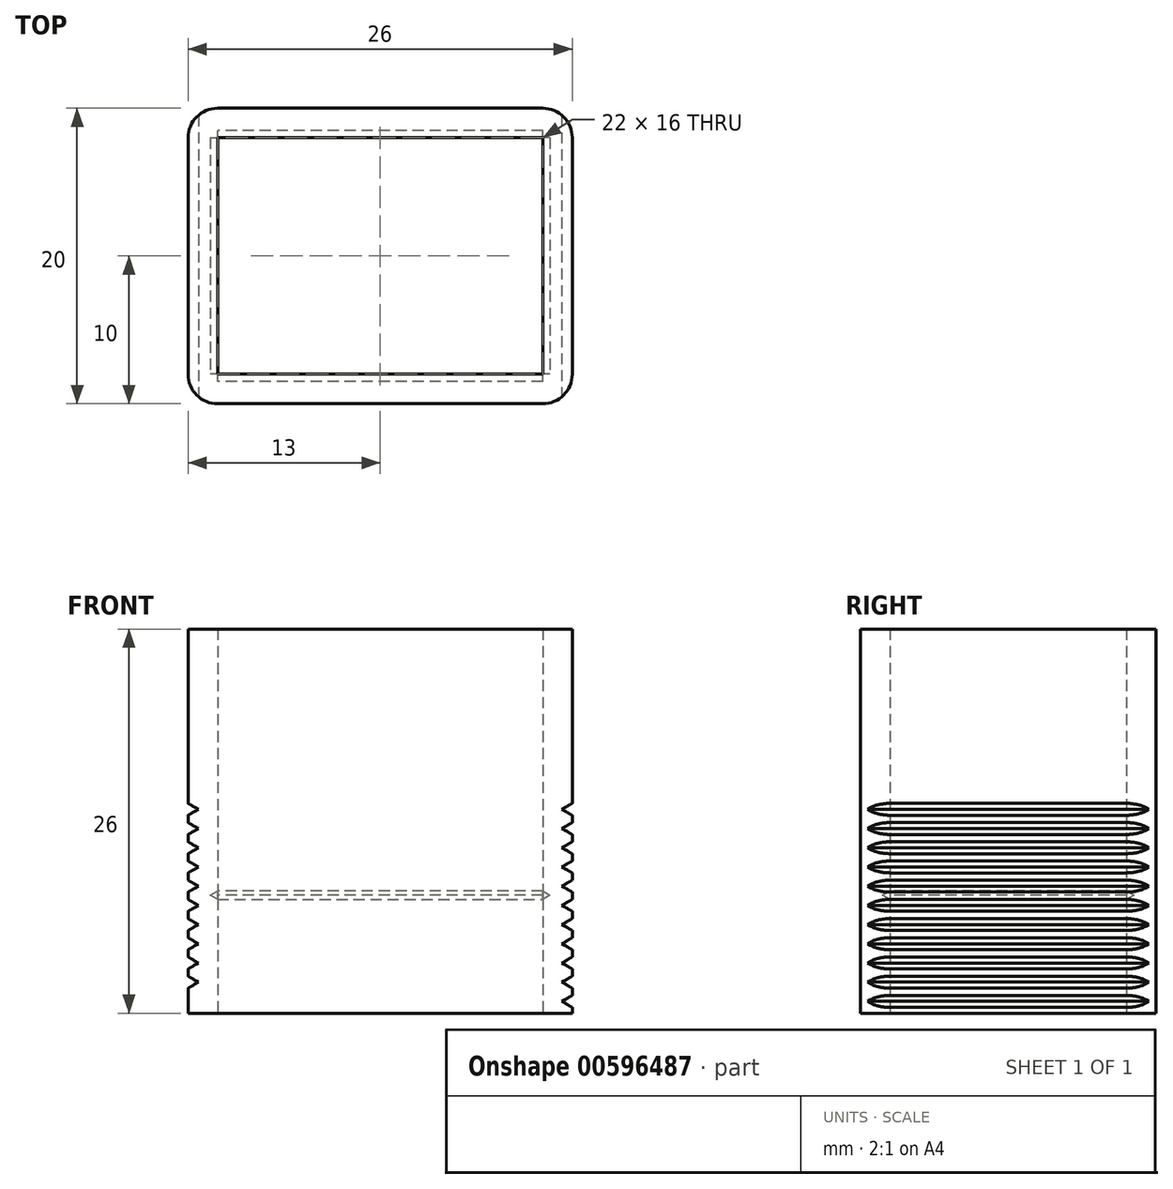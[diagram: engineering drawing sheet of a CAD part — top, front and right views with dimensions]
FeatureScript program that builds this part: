
annotation { "Feature Type Name" : "Feature", "Feature Type Description" : "" }
export const myFeature = defineFeature(function(context is Context, id is Id, definition is map)
    precondition{}
    {
        {
            var Q0;
            Q0=qCreatedBy(makeId("Top.planeOp"),FACE);
            var sketch = newSketch(context, id + "F0", { "sketchPlane" : qUnion([Q0])});
            skLineSegment(sketch, "E0.bottom", {"start": v(0, 0) * mm, "end": v(22, 0) * mm});
            skLineSegment(sketch, "E0.top", {"start": v(0, 16) * mm, "end": v(22, 16) * mm});
            skLineSegment(sketch, "E0.left", {"start": v(0, 0) * mm, "end": v(0, 16) * mm});
            skLineSegment(sketch, "E0.right", {"start": v(22, 0) * mm, "end": v(22, 16) * mm});
            skSolve(sketch);
        }
        {
            var Q0;
            Q0=makeQuery(id+"F0.imprint","IMPRINT",FACE,{"disambiguationData":[TD([[makeQuery(id+"F0.imprint","IMPRINT",EDGE,{"derivedFrom":sQuery(id+"F0.wireOp",EDGE,"E0.bottom")}),1.0]])]});
            extrude(context, id + "F1", {"entities" : qUnion([Q0]), "depth" : 28 * mm, "offsetDistance" : 25 * mm, "hasSecondDirection" : true, "secondDirectionOppositeDirection" : false, "secondDirectionDepth" : 4 * mm});
        }
        {
            var Q0;
            Q0=makeQuery(id+"F1.opExtrude","CAP_FACE",FACE,{"disambiguationData":[OSD([sQuery(id+"F0.wireOp",EDGE,"E0.bottom"),sQuery(id+"F0.wireOp",EDGE,"E0.top"),sQuery(id+"F0.wireOp",EDGE,"E0.left"),sQuery(id+"F0.wireOp",EDGE,"E0.right")])],"isStart":false});
            shell(context, id + "F2", {"entities" : qUnion([Q0]), "thickness" : 2 * mm, "oppositeDirection" : true});
        }
        {
            var Q0;
            Q0=makeQuery(id+"F1.opExtrude","SWEPT_FACE",FACE,{"disambiguationData":[OSD([sQuery(id+"F0.wireOp",EDGE,"E0.left")])]});
            var sketch = newSketch(context, id + "F3", { "sketchPlane" : qUnion([Q0])});
            skLineSegment(sketch, "E1.0", {"start": v(-16, 28) * mm, "end": v(-16, 4) * mm});
            skLineSegment(sketch, "E2.0", {"start": v(0, 28) * mm, "end": v(0, 4) * mm});
            skLineSegment(sketch, "E3.0", {"start": v(0, 0) * mm, "end": v(-16, 0) * mm});
            skLineSegment(sketch, "E4", {"start": v(-16, 10) * mm, "end": v(0, 10) * mm});
            skCircle(sketch, "E5.cCircle", {"center": v(-16, 10) * mm, "radius": 0.25 * mm, "construction": true});
            skLineSegment(sketch, "E5.0", {"start": v(-15.75, 10.43) * mm, "end": v(-15.75, 9.57) * mm});
            skLineSegment(sketch, "E5.1", {"start": v(-15.75, 9.57) * mm, "end": v(-16.5, 10) * mm});
            skLineSegment(sketch, "E5.2", {"start": v(-16.5, 10) * mm, "end": v(-15.75, 10.43) * mm});
            skPoint(sketch, "E5.0.midPoint", {"position": v(-15.75, 10) * mm});
            skCircle(sketch, "E6.cCircle", {"center": v(0, 10) * mm, "radius": 0.25 * mm, "construction": true});
            skLineSegment(sketch, "E6.0", {"start": v(-0.25, 9.57) * mm, "end": v(-0.25, 10.43) * mm});
            skLineSegment(sketch, "E6.1", {"start": v(-0.25, 10.43) * mm, "end": v(0.5, 10) * mm});
            skLineSegment(sketch, "E6.2", {"start": v(0.5, 10) * mm, "end": v(-0.25, 9.57) * mm});
            skPoint(sketch, "E6.0.midPoint", {"position": v(-0.25, 10) * mm});
            skSolve(sketch);
        }
        {
            var Q0;
            {var subQ0=sQuery(id+"F3.wireOp",EDGE,"E1.0");var subQ1=makeQuery(id+"F3.imprint","INTERSECT",VERTEX,{"derivedFrom":[subQ0,sQuery(id+"F3.wireOp",EDGE,"E4")]});Q0=makeQuery(id+"F3.imprint","IMPRINT",FACE,{"disambiguationData":[TD([[makeQuery(id+"F3.imprint","IMPRINT",EDGE,{"disambiguationData":[TD([[subQ1,1.0]])],"derivedFrom":subQ0}),-1.0]])]});}
            var Q1;
            {var subQ0=sQuery(id+"F3.wireOp",EDGE,"E4");var subQ1=sQuery(id+"F3.wireOp",EDGE,"E1.0");var subQ2=makeQuery(id+"F3.imprint","INTERSECT",VERTEX,{"derivedFrom":[subQ1,subQ0]});Q1=makeQuery(id+"F3.imprint","IMPRINT",FACE,{"disambiguationData":[TD([[makeQuery(id+"F3.imprint","IMPRINT",EDGE,{"disambiguationData":[TD([[subQ2,1.0]])],"derivedFrom":subQ1}),1.0]])]});}
            var Q2;
            {var subQ0=sQuery(id+"F3.wireOp",EDGE,"E4");var subQ1=sQuery(id+"F3.wireOp",EDGE,"E1.0");var subQ2=makeQuery(id+"F3.imprint","INTERSECT",VERTEX,{"derivedFrom":[subQ1,subQ0]});Q2=makeQuery(id+"F3.imprint","IMPRINT",FACE,{"disambiguationData":[TD([[makeQuery(id+"F3.imprint","IMPRINT",EDGE,{"disambiguationData":[TD([[subQ2,-1.0]])],"derivedFrom":subQ1}),1.0]])]});}
            var Q3;
            {var subQ0=sQuery(id+"F3.wireOp",EDGE,"E4");var subQ1=sQuery(id+"F3.wireOp",EDGE,"E2.0");var subQ2=makeQuery(id+"F3.imprint","INTERSECT",VERTEX,{"derivedFrom":[subQ1,subQ0]});Q3=makeQuery(id+"F3.imprint","IMPRINT",FACE,{"disambiguationData":[TD([[makeQuery(id+"F3.imprint","IMPRINT",EDGE,{"disambiguationData":[TD([[subQ2,1.0]])],"derivedFrom":subQ1}),-1.0]])]});}
            var Q4;
            {var subQ0=sQuery(id+"F3.wireOp",EDGE,"E4");var subQ1=sQuery(id+"F3.wireOp",EDGE,"E2.0");var subQ2=makeQuery(id+"F3.imprint","INTERSECT",VERTEX,{"derivedFrom":[subQ1,subQ0]});Q4=makeQuery(id+"F3.imprint","IMPRINT",FACE,{"disambiguationData":[TD([[makeQuery(id+"F3.imprint","IMPRINT",EDGE,{"disambiguationData":[TD([[subQ2,-1.0]])],"derivedFrom":subQ1}),-1.0]])]});}
            var Q5;
            {var subQ0=sQuery(id+"F3.wireOp",EDGE,"E2.0");var subQ1=makeQuery(id+"F3.imprint","INTERSECT",VERTEX,{"derivedFrom":[subQ0,sQuery(id+"F3.wireOp",EDGE,"E4")]});Q5=makeQuery(id+"F3.imprint","IMPRINT",FACE,{"disambiguationData":[TD([[makeQuery(id+"F3.imprint","IMPRINT",EDGE,{"disambiguationData":[TD([[subQ1,1.0]])],"derivedFrom":subQ0}),1.0]])]});}
            var Q6;
            Q6=makeQuery(id+"F2.opShell","OFFSET_FACE",FACE,{"disambiguationData":[OSD([sQuery(id+"F0.wireOp",EDGE,"E0.right")])]});
            var Q7;
            Q7=makeQuery(id+"F2.opShell","OFFSET_FACE",FACE,{"disambiguationData":[OSD([sQuery(id+"F0.wireOp",EDGE,"E0.left")])]});
            extrude(context, id + "F4", {"entities" : qUnion([Q0, Q1, Q2, Q3, Q4, Q5]), "operationType" : NewBodyOperationType.REMOVE, "endBound" : BoundingType.UP_TO_SURFACE, "oppositeDirection" : true, "depth" : 25 * mm, "endBoundEntityFace" : qUnion([Q6]), "offsetDistance" : 25 * mm, "hasSecondDirection" : true, "secondDirectionBound" : BoundingType.UP_TO_SURFACE, "secondDirectionOppositeDirection" : true, "secondDirectionDepth" : 25 * mm, "secondDirectionBoundEntityFace" : qUnion([Q7])});
        }
        {
            var Q0;
            Q0=makeQuery(id+"F1.opExtrude","SWEPT_FACE",FACE,{"disambiguationData":[OSD([sQuery(id+"F0.wireOp",EDGE,"E0.bottom")])]});
            var sketch = newSketch(context, id + "F5", { "sketchPlane" : qUnion([Q0])});
            skLineSegment(sketch, "E7.0", {"start": v(0, 9.71) * mm, "end": v(0, 10) * mm});
            skLineSegment(sketch, "E8.0", {"start": v(0, 10) * mm, "end": v(0, 10.29) * mm});
            skLineSegment(sketch, "E9.0", {"start": v(22, 9.71) * mm, "end": v(22, 10) * mm});
            skLineSegment(sketch, "E10.0", {"start": v(22, 10) * mm, "end": v(22, 10.29) * mm});
            skLineSegment(sketch, "E11.0", {"start": v(22, 10) * mm, "end": v(0, 10) * mm});
            skCircle(sketch, "E12.cCircle", {"center": v(0, 10) * mm, "radius": 0.25 * mm, "construction": true});
            skLineSegment(sketch, "E12.0", {"start": v(0.25, 10.43) * mm, "end": v(0.25, 9.57) * mm});
            skLineSegment(sketch, "E12.1", {"start": v(0.25, 9.57) * mm, "end": v(-0.5, 10) * mm});
            skLineSegment(sketch, "E12.2", {"start": v(-0.5, 10) * mm, "end": v(0.25, 10.43) * mm});
            skPoint(sketch, "E12.0.midPoint", {"position": v(0.25, 10) * mm});
            skCircle(sketch, "E13.cCircle", {"center": v(22, 10) * mm, "radius": 0.25 * mm, "construction": true});
            skLineSegment(sketch, "E13.0", {"start": v(21.75, 9.57) * mm, "end": v(21.75, 10.43) * mm});
            skLineSegment(sketch, "E13.1", {"start": v(21.75, 10.43) * mm, "end": v(22.5, 10) * mm});
            skLineSegment(sketch, "E13.2", {"start": v(22.5, 10) * mm, "end": v(21.75, 9.57) * mm});
            skPoint(sketch, "E13.0.midPoint", {"position": v(21.75, 10) * mm});
            skLineSegment(sketch, "E14", {"start": v(24, 8) * mm, "end": v(-2, 8) * mm, "construction": true});
            skCircle(sketch, "E15.cCircle", {"center": v(-2, 8) * mm, "radius": 0.35 * mm, "construction": true});
            skLineSegment(sketch, "E15.0", {"start": v(-2.35, 7.4) * mm, "end": v(-2.35, 8.6) * mm});
            skLineSegment(sketch, "E15.1", {"start": v(-2.35, 8.6) * mm, "end": v(-1.3, 8) * mm});
            skLineSegment(sketch, "E15.2", {"start": v(-1.3, 8) * mm, "end": v(-2.35, 7.4) * mm});
            skPoint(sketch, "E15.0.midPoint", {"position": v(-2.35, 8) * mm});
            skLineSegment(sketch, "E16.0", {"start": v(-2, 28) * mm, "end": v(-2, 4) * mm});
            skLineSegment(sketch, "E17.0.1.0", {"start": v(-2.35, 8.7) * mm, "end": v(-2.35, 9.9) * mm});
            skCircle(sketch, "E17.0.1.1", {"center": v(-2, 9.3) * mm, "radius": 0.35 * mm, "construction": true});
            skPoint(sketch, "E17.0.1.2", {"position": v(-2.35, 9.3) * mm});
            skLineSegment(sketch, "E17.0.1.3", {"start": v(-1.3, 9.3) * mm, "end": v(-2.35, 8.7) * mm});
            skLineSegment(sketch, "E17.0.1.4", {"start": v(-2.35, 9.9) * mm, "end": v(-1.3, 9.3) * mm});
            skLineSegment(sketch, "E17.0.2.0", {"start": v(-2.35, 10) * mm, "end": v(-2.35, 11.2) * mm});
            skCircle(sketch, "E17.0.2.1", {"center": v(-2, 10.6) * mm, "radius": 0.35 * mm, "construction": true});
            skPoint(sketch, "E17.0.2.2", {"position": v(-2.35, 10.6) * mm});
            skLineSegment(sketch, "E17.0.2.3", {"start": v(-1.3, 10.6) * mm, "end": v(-2.35, 10) * mm});
            skLineSegment(sketch, "E17.0.2.4", {"start": v(-2.35, 11.2) * mm, "end": v(-1.3, 10.6) * mm});
            skLineSegment(sketch, "E17.0.3.0", {"start": v(-2.35, 11.3) * mm, "end": v(-2.35, 12.5) * mm});
            skCircle(sketch, "E17.0.3.1", {"center": v(-2, 11.9) * mm, "radius": 0.35 * mm, "construction": true});
            skPoint(sketch, "E17.0.3.2", {"position": v(-2.35, 11.9) * mm});
            skLineSegment(sketch, "E17.0.3.3", {"start": v(-1.3, 11.9) * mm, "end": v(-2.35, 11.3) * mm});
            skLineSegment(sketch, "E17.0.3.4", {"start": v(-2.35, 12.5) * mm, "end": v(-1.3, 11.9) * mm});
            skLineSegment(sketch, "E17.0.4.0", {"start": v(-2.35, 12.6) * mm, "end": v(-2.35, 13.8) * mm});
            skCircle(sketch, "E17.0.4.1", {"center": v(-2, 13.2) * mm, "radius": 0.35 * mm, "construction": true});
            skPoint(sketch, "E17.0.4.2", {"position": v(-2.35, 13.2) * mm});
            skLineSegment(sketch, "E17.0.4.3", {"start": v(-1.3, 13.2) * mm, "end": v(-2.35, 12.6) * mm});
            skLineSegment(sketch, "E17.0.4.4", {"start": v(-2.35, 13.8) * mm, "end": v(-1.3, 13.2) * mm});
            skLineSegment(sketch, "E17.0.5.0", {"start": v(-2.35, 13.9) * mm, "end": v(-2.35, 15.1) * mm});
            skCircle(sketch, "E17.0.5.1", {"center": v(-2, 14.5) * mm, "radius": 0.35 * mm, "construction": true});
            skPoint(sketch, "E17.0.5.2", {"position": v(-2.35, 14.5) * mm});
            skLineSegment(sketch, "E17.0.5.3", {"start": v(-1.3, 14.5) * mm, "end": v(-2.35, 13.9) * mm});
            skLineSegment(sketch, "E17.0.5.4", {"start": v(-2.35, 15.1) * mm, "end": v(-1.3, 14.5) * mm});
            skLineSegment(sketch, "E17.direction1", {"start": v(-2.35, 8) * mm, "end": v(1.16, 8) * mm, "construction": true});
            skLineSegment(sketch, "E17.direction2", {"start": v(-2.35, 8) * mm, "end": v(-2.35, 9.3) * mm, "construction": true});
            skLineSegment(sketch, "E18.0.0.6", {"start": v(-2.35, 15.2) * mm, "end": v(-2.35, 16.4) * mm});
            skCircle(sketch, "E18.3.0.6", {"center": v(-2, 15.8) * mm, "radius": 0.35 * mm, "construction": true});
            skPoint(sketch, "E18.5.0.6", {"position": v(-2.35, 15.8) * mm});
            skLineSegment(sketch, "E18.6.0.6", {"start": v(-1.3, 15.8) * mm, "end": v(-2.35, 15.2) * mm});
            skLineSegment(sketch, "E18.9.0.6", {"start": v(-2.35, 16.4) * mm, "end": v(-1.3, 15.8) * mm});
            skLineSegment(sketch, "E19.MirrorCS", {"start": v(-1.3, 5.4) * mm, "end": v(-2.35, 6) * mm});
            skLineSegment(sketch, "E20.MirrorCS", {"start": v(-1.3, 4.1) * mm, "end": v(-2.35, 4.7) * mm});
            skLineSegment(sketch, "E21.MirrorCS", {"start": v(-2.35, 4.8) * mm, "end": v(-1.3, 5.4) * mm});
            skLineSegment(sketch, "E22.MirrorCS", {"start": v(-2.35, 6.1) * mm, "end": v(-1.3, 6.7) * mm});
            skLineSegment(sketch, "E23.MirrorCS", {"start": v(-2.35, 3.5) * mm, "end": v(-1.3, 4.1) * mm});
            skLineSegment(sketch, "E24.MirrorCS", {"start": v(-2.35, 2.2) * mm, "end": v(-1.3, 2.8) * mm});
            skLineSegment(sketch, "E25.MirrorCS", {"start": v(-2.35, 2.1) * mm, "end": v(-2.35, 0.9) * mm});
            skLineSegment(sketch, "E26.MirrorCS", {"start": v(-2.35, 0.8) * mm, "end": v(-2.35, -0.4) * mm});
            skLineSegment(sketch, "E27.MirrorCS", {"start": v(-1.3, 0.2) * mm, "end": v(-2.35, 0.8) * mm});
            skLineSegment(sketch, "E28.MirrorCS", {"start": v(-2.35, 4.7) * mm, "end": v(-2.35, 3.5) * mm});
            skCircle(sketch, "E29.MirrorC", {"center": v(-2, 6.7) * mm, "radius": 0.35 * mm, "construction": true});
            skCircle(sketch, "E30.MirrorC", {"center": v(-2, 1.5) * mm, "radius": 0.35 * mm, "construction": true});
            skCircle(sketch, "E31.MirrorC", {"center": v(-2, 5.4) * mm, "radius": 0.35 * mm, "construction": true});
            skLineSegment(sketch, "E32.MirrorCS", {"start": v(-2.35, 3.4) * mm, "end": v(-2.35, 2.2) * mm});
            skCircle(sketch, "E33.MirrorC", {"center": v(-2, 4.1) * mm, "radius": 0.35 * mm, "construction": true});
            skLineSegment(sketch, "E34.MirrorCS", {"start": v(-2.35, 0.9) * mm, "end": v(-1.3, 1.5) * mm});
            skLineSegment(sketch, "E35.MirrorCS", {"start": v(-1.3, 2.8) * mm, "end": v(-2.35, 3.4) * mm});
            skLineSegment(sketch, "E36.MirrorCS", {"start": v(-2.35, 6) * mm, "end": v(-2.35, 4.8) * mm});
            skLineSegment(sketch, "E37.MirrorCS", {"start": v(-1.3, 6.7) * mm, "end": v(-2.35, 7.3) * mm});
            skCircle(sketch, "E38.MirrorC", {"center": v(-2, 0.2) * mm, "radius": 0.35 * mm, "construction": true});
            skLineSegment(sketch, "E39.MirrorCS", {"start": v(-2.35, 7.3) * mm, "end": v(-2.35, 6.1) * mm});
            skPoint(sketch, "E40.MirrorP", {"position": v(-2.35, 0.2) * mm});
            skCircle(sketch, "E41.MirrorC", {"center": v(-2, 2.8) * mm, "radius": 0.35 * mm, "construction": true});
            skPoint(sketch, "E42.MirrorP", {"position": v(-2.35, 1.5) * mm});
            skPoint(sketch, "E43.MirrorP", {"position": v(-2.35, 6.7) * mm});
            skPoint(sketch, "E44.MirrorP", {"position": v(-2.35, 5.4) * mm});
            skLineSegment(sketch, "E45.MirrorCS", {"start": v(-2.35, -0.4) * mm, "end": v(-1.3, 0.2) * mm});
            skLineSegment(sketch, "E46.MirrorCS", {"start": v(-1.3, 1.5) * mm, "end": v(-2.35, 2.1) * mm});
            skPoint(sketch, "E47.MirrorP", {"position": v(-2.35, 2.8) * mm});
            skPoint(sketch, "E48.MirrorP", {"position": v(-2.35, 4.1) * mm});
            skLineSegment(sketch, "E49", {"start": v(11, 18) * mm, "end": v(11, -2) * mm, "construction": true});
            skLineSegment(sketch, "E50.MirrorCS", {"start": v(24.35, 11.3) * mm, "end": v(24.35, 12.5) * mm});
            skLineSegment(sketch, "E51.MirrorCS", {"start": v(24.35, 8.7) * mm, "end": v(24.35, 9.9) * mm});
            skLineSegment(sketch, "E52.MirrorCS", {"start": v(24.35, 10) * mm, "end": v(24.35, 11.2) * mm});
            skLineSegment(sketch, "E53.MirrorCS", {"start": v(24.35, 4.7) * mm, "end": v(24.35, 3.5) * mm});
            skLineSegment(sketch, "E54.MirrorCS", {"start": v(24.35, 6) * mm, "end": v(24.35, 4.8) * mm});
            skLineSegment(sketch, "E55.MirrorCS", {"start": v(24.35, 12.6) * mm, "end": v(24.35, 13.8) * mm});
            skLineSegment(sketch, "E56.MirrorCS", {"start": v(24.35, 7.4) * mm, "end": v(24.35, 8.6) * mm});
            skLineSegment(sketch, "E57.MirrorCS", {"start": v(23.3, 11.9) * mm, "end": v(24.35, 11.3) * mm});
            skCircle(sketch, "E58.MirrorC", {"center": v(24, 11.9) * mm, "radius": 0.35 * mm, "construction": true});
            skLineSegment(sketch, "E59.MirrorCS", {"start": v(24.35, 8.6) * mm, "end": v(23.3, 8) * mm});
            skCircle(sketch, "E60.MirrorC", {"center": v(24, 10.6) * mm, "radius": 0.35 * mm, "construction": true});
            skLineSegment(sketch, "E61.MirrorCS", {"start": v(24.35, 7.3) * mm, "end": v(24.35, 6.1) * mm});
            skLineSegment(sketch, "E62.MirrorCS", {"start": v(24.35, 8) * mm, "end": v(24.35, 9.3) * mm, "construction": true});
            skCircle(sketch, "E63.MirrorC", {"center": v(24, 8) * mm, "radius": 0.35 * mm, "construction": true});
            skLineSegment(sketch, "E64.MirrorCS", {"start": v(23.3, 10.6) * mm, "end": v(24.35, 10) * mm});
            skCircle(sketch, "E65.MirrorC", {"center": v(24, 2.8) * mm, "radius": 0.35 * mm, "construction": true});
            skLineSegment(sketch, "E66.MirrorCS", {"start": v(24.35, 2.2) * mm, "end": v(23.3, 2.8) * mm});
            skLineSegment(sketch, "E67.MirrorCS", {"start": v(24.35, 13.8) * mm, "end": v(23.3, 13.2) * mm});
            skCircle(sketch, "E68.MirrorC", {"center": v(24, 4.1) * mm, "radius": 0.35 * mm, "construction": true});
            skLineSegment(sketch, "E69.MirrorCS", {"start": v(23.3, 15.8) * mm, "end": v(24.35, 15.2) * mm});
            skLineSegment(sketch, "E70.MirrorCS", {"start": v(24.35, -0.4) * mm, "end": v(23.3, 0.2) * mm});
            skLineSegment(sketch, "E71.MirrorCS", {"start": v(24.35, 2.1) * mm, "end": v(24.35, 0.9) * mm});
            skLineSegment(sketch, "E72.MirrorCS", {"start": v(24.35, 13.9) * mm, "end": v(24.35, 15.1) * mm});
            skCircle(sketch, "E73.MirrorC", {"center": v(24, 9.3) * mm, "radius": 0.35 * mm, "construction": true});
            skLineSegment(sketch, "E74.MirrorCS", {"start": v(23.3, 1.5) * mm, "end": v(24.35, 2.1) * mm});
            skLineSegment(sketch, "E75.MirrorCS", {"start": v(23.3, 2.8) * mm, "end": v(24.35, 3.4) * mm});
            skLineSegment(sketch, "E76.MirrorCS", {"start": v(23.3, 5.4) * mm, "end": v(24.35, 6) * mm});
            skPoint(sketch, "E77.MirrorP", {"position": v(24.35, 4.1) * mm});
            skLineSegment(sketch, "E78.MirrorCS", {"start": v(24.35, 11.2) * mm, "end": v(23.3, 10.6) * mm});
            skPoint(sketch, "E79.MirrorP", {"position": v(24.35, 13.2) * mm});
            skLineSegment(sketch, "E80.MirrorCS", {"start": v(24.35, 3.4) * mm, "end": v(24.35, 2.2) * mm});
            skLineSegment(sketch, "E81.MirrorCS", {"start": v(24.35, 0.8) * mm, "end": v(24.35, -0.4) * mm});
            skCircle(sketch, "E82.MirrorC", {"center": v(24, 14.5) * mm, "radius": 0.35 * mm, "construction": true});
            skLineSegment(sketch, "E83.MirrorCS", {"start": v(23.3, 14.5) * mm, "end": v(24.35, 13.9) * mm});
            skLineSegment(sketch, "E84.MirrorCS", {"start": v(24.35, 0.9) * mm, "end": v(23.3, 1.5) * mm});
            skLineSegment(sketch, "E85.MirrorCS", {"start": v(24.35, 3.5) * mm, "end": v(23.3, 4.1) * mm});
            skPoint(sketch, "E86.MirrorP", {"position": v(24.35, 6.7) * mm});
            skLineSegment(sketch, "E87.MirrorCS", {"start": v(24.35, 15.1) * mm, "end": v(23.3, 14.5) * mm});
            skCircle(sketch, "E88.MirrorC", {"center": v(24, 15.8) * mm, "radius": 0.35 * mm, "construction": true});
            skLineSegment(sketch, "E89.MirrorCS", {"start": v(24.35, 9.9) * mm, "end": v(23.3, 9.3) * mm});
            skCircle(sketch, "E90.MirrorC", {"center": v(24, 1.5) * mm, "radius": 0.35 * mm, "construction": true});
            skLineSegment(sketch, "E91.MirrorCS", {"start": v(24.35, 15.2) * mm, "end": v(24.35, 16.4) * mm});
            skCircle(sketch, "E92.MirrorC", {"center": v(24, 6.7) * mm, "radius": 0.35 * mm, "construction": true});
            skLineSegment(sketch, "E93.MirrorCS", {"start": v(23.3, 4.1) * mm, "end": v(24.35, 4.7) * mm});
            skLineSegment(sketch, "E94.MirrorCS", {"start": v(23.3, 0.2) * mm, "end": v(24.35, 0.8) * mm});
            skLineSegment(sketch, "E95.MirrorCS", {"start": v(23.3, 13.2) * mm, "end": v(24.35, 12.6) * mm});
            skCircle(sketch, "E96.MirrorC", {"center": v(24, 5.4) * mm, "radius": 0.35 * mm, "construction": true});
            skCircle(sketch, "E97.MirrorC", {"center": v(24, 13.2) * mm, "radius": 0.35 * mm, "construction": true});
            skLineSegment(sketch, "E98.MirrorCS", {"start": v(23.3, 9.3) * mm, "end": v(24.35, 8.7) * mm});
            skPoint(sketch, "E99.MirrorP", {"position": v(24.35, 5.4) * mm});
            skPoint(sketch, "E100.MirrorP", {"position": v(24.35, 11.9) * mm});
            skPoint(sketch, "E101.MirrorP", {"position": v(24.35, 10.6) * mm});
            skLineSegment(sketch, "E102.MirrorCS", {"start": v(24.35, 12.5) * mm, "end": v(23.3, 11.9) * mm});
            skLineSegment(sketch, "E103.MirrorCS", {"start": v(24.35, 6.1) * mm, "end": v(23.3, 6.7) * mm});
            skLineSegment(sketch, "E104.MirrorCS", {"start": v(23.3, 6.7) * mm, "end": v(24.35, 7.3) * mm});
            skLineSegment(sketch, "E105.MirrorCS", {"start": v(24.35, 4.8) * mm, "end": v(23.3, 5.4) * mm});
            skCircle(sketch, "E106.MirrorC", {"center": v(24, 0.2) * mm, "radius": 0.35 * mm, "construction": true});
            skLineSegment(sketch, "E107.MirrorCS", {"start": v(23.3, 8) * mm, "end": v(24.35, 7.4) * mm});
            skLineSegment(sketch, "E108.MirrorCS", {"start": v(24.35, 16.4) * mm, "end": v(23.3, 15.8) * mm});
            skPoint(sketch, "E109.MirrorP", {"position": v(24.35, 14.5) * mm});
            skPoint(sketch, "E110.MirrorP", {"position": v(24.35, 8) * mm});
            skPoint(sketch, "E111.MirrorP", {"position": v(24.35, 0.2) * mm});
            skPoint(sketch, "E112.MirrorP", {"position": v(24.35, 1.5) * mm});
            skPoint(sketch, "E113.MirrorP", {"position": v(24.35, 2.8) * mm});
            skPoint(sketch, "E114.MirrorP", {"position": v(24.35, 15.8) * mm});
            skPoint(sketch, "E115.MirrorP", {"position": v(24.35, 9.3) * mm});
            skSolve(sketch);
        }
        {
            var Q0;
            {var subQ0=sQuery(id+"F5.wireOp",EDGE,"E7.0");Q0=makeQuery(id+"F5.imprint","IMPRINT",FACE,{"disambiguationData":[TD([[makeQuery(id+"F5.imprint","IMPRINT",EDGE,{"derivedFrom":subQ0}),1.0]])]});}
            var Q1;
            {var subQ0=sQuery(id+"F5.wireOp",EDGE,"E8.0");Q1=makeQuery(id+"F5.imprint","IMPRINT",FACE,{"disambiguationData":[TD([[makeQuery(id+"F5.imprint","IMPRINT",EDGE,{"derivedFrom":subQ0}),-1.0]])]});}
            var Q2;
            {var subQ0=sQuery(id+"F5.wireOp",EDGE,"E7.0");Q2=makeQuery(id+"F5.imprint","IMPRINT",FACE,{"disambiguationData":[TD([[makeQuery(id+"F5.imprint","IMPRINT",EDGE,{"derivedFrom":subQ0}),-1.0]])]});}
            var Q3;
            {var subQ0=sQuery(id+"F5.wireOp",EDGE,"E9.0");Q3=makeQuery(id+"F5.imprint","IMPRINT",FACE,{"disambiguationData":[TD([[makeQuery(id+"F5.imprint","IMPRINT",EDGE,{"derivedFrom":subQ0}),-1.0]])]});}
            var Q4;
            {var subQ0=sQuery(id+"F5.wireOp",EDGE,"E10.0");Q4=makeQuery(id+"F5.imprint","IMPRINT",FACE,{"disambiguationData":[TD([[makeQuery(id+"F5.imprint","IMPRINT",EDGE,{"derivedFrom":subQ0}),1.0]])]});}
            var Q5;
            {var subQ0=sQuery(id+"F5.wireOp",EDGE,"E9.0");Q5=makeQuery(id+"F5.imprint","IMPRINT",FACE,{"disambiguationData":[TD([[makeQuery(id+"F5.imprint","IMPRINT",EDGE,{"derivedFrom":subQ0}),1.0]])]});}
            var Q6;
            {var subQ2=sQuery(id+"F0.wireOp",EDGE,"E0.top");Q6=makeQuery(id+"F4.boolean.opBoolean","SPLIT",FACE,{"disambiguationData":[TD([makeQuery(id+"F4.opExtrude","SWEPT_FACE",FACE,{"disambiguationData":[OSD([sQuery(id+"F3.wireOp",EDGE,"E5.2")])]})])],"derivedFrom":makeQuery(id+"F2.opShell","OFFSET_FACE",FACE,{"disambiguationData":[OSD([subQ2])]})});}
            var Q7;
            {var subQ2=sQuery(id+"F0.wireOp",EDGE,"E0.bottom");Q7=makeQuery(id+"F4.boolean.opBoolean","SPLIT",FACE,{"disambiguationData":[TD([makeQuery(id+"F4.opExtrude","SWEPT_FACE",FACE,{"disambiguationData":[OSD([sQuery(id+"F3.wireOp",EDGE,"E6.1")])]})])],"derivedFrom":makeQuery(id+"F2.opShell","OFFSET_FACE",FACE,{"disambiguationData":[OSD([subQ2])]})});}
            extrude(context, id + "F6", {"entities" : qUnion([Q0, Q1, Q2, Q3, Q4, Q5]), "operationType" : NewBodyOperationType.REMOVE, "endBound" : BoundingType.UP_TO_SURFACE, "oppositeDirection" : true, "depth" : 25 * mm, "endBoundEntityFace" : qUnion([Q6]), "offsetDistance" : 25 * mm, "hasSecondDirection" : true, "secondDirectionBound" : BoundingType.UP_TO_SURFACE, "secondDirectionOppositeDirection" : true, "secondDirectionDepth" : 25 * mm, "secondDirectionBoundEntityFace" : qUnion([Q7])});
        }
        {
            var Q0;
            Q0=makeQuery(id+"F1.opExtrude","SWEPT_EDGE",EDGE,{"disambiguationData":[OSD([sQuery(id+"F0.wireOp",EDGE,"E0.bottom"),sQuery(id+"F0.wireOp",EDGE,"E0.right")])]});
            var Q1;
            Q1=makeQuery(id+"F1.opExtrude","SWEPT_EDGE",EDGE,{"disambiguationData":[OSD([sQuery(id+"F0.wireOp",EDGE,"E0.top"),sQuery(id+"F0.wireOp",EDGE,"E0.right")])]});
            var Q2;
            Q2=makeQuery(id+"F1.opExtrude","SWEPT_EDGE",EDGE,{"disambiguationData":[OSD([sQuery(id+"F0.wireOp",EDGE,"E0.bottom"),sQuery(id+"F0.wireOp",EDGE,"E0.left")])]});
            var Q3;
            Q3=makeQuery(id+"F1.opExtrude","SWEPT_EDGE",EDGE,{"disambiguationData":[OSD([sQuery(id+"F0.wireOp",EDGE,"E0.top"),sQuery(id+"F0.wireOp",EDGE,"E0.left")])]});
            fillet(context, id + "F7", {"entities" : qUnion([Q0, Q1, Q2, Q3]), "radius" : 2 * mm, "tangentPropagation" : true, "allowEdgeOverflow" : false});
        }
        {
            var Q0;
            {var subQ0=sQuery(id+"F5.wireOp",EDGE,"E108.MirrorCS");var subQ1=sQuery(id+"F5.wireOp",EDGE,"E69.MirrorCS");var subQ2=makeQuery(id+"F5.imprint","INTERSECT",VERTEX,{"derivedFrom":[subQ1,subQ0]});Q0=makeQuery(id+"F5.imprint","IMPRINT",FACE,{"disambiguationData":[TD([[makeQuery(id+"F5.imprint","IMPRINT",EDGE,{"disambiguationData":[TD([[subQ2,-1.0]])],"derivedFrom":subQ1}),1.0]])]});}
            var Q1;
            {var subQ0=sQuery(id+"F5.wireOp",EDGE,"E91.MirrorCS");Q1=makeQuery(id+"F5.imprint","IMPRINT",FACE,{"disambiguationData":[TD([[makeQuery(id+"F5.imprint","IMPRINT",EDGE,{"derivedFrom":subQ0}),1.0]])]});}
            var Q2;
            {var subQ0=sQuery(id+"F5.wireOp",EDGE,"E87.MirrorCS");var subQ1=sQuery(id+"F5.wireOp",EDGE,"E83.MirrorCS");var subQ2=makeQuery(id+"F5.imprint","INTERSECT",VERTEX,{"derivedFrom":[subQ1,subQ0]});Q2=makeQuery(id+"F5.imprint","IMPRINT",FACE,{"disambiguationData":[TD([[makeQuery(id+"F5.imprint","IMPRINT",EDGE,{"disambiguationData":[TD([[subQ2,-1.0]])],"derivedFrom":subQ1}),1.0]])]});}
            var Q3;
            {var subQ0=sQuery(id+"F5.wireOp",EDGE,"E72.MirrorCS");Q3=makeQuery(id+"F5.imprint","IMPRINT",FACE,{"disambiguationData":[TD([[makeQuery(id+"F5.imprint","IMPRINT",EDGE,{"derivedFrom":subQ0}),1.0]])]});}
            var Q4;
            {var subQ0=sQuery(id+"F5.wireOp",EDGE,"E95.MirrorCS");var subQ1=sQuery(id+"F5.wireOp",EDGE,"E67.MirrorCS");var subQ2=makeQuery(id+"F5.imprint","INTERSECT",VERTEX,{"derivedFrom":[subQ1,subQ0]});Q4=makeQuery(id+"F5.imprint","IMPRINT",FACE,{"disambiguationData":[TD([[makeQuery(id+"F5.imprint","IMPRINT",EDGE,{"disambiguationData":[TD([[subQ2,1.0]])],"derivedFrom":subQ1}),1.0]])]});}
            var Q5;
            {var subQ0=sQuery(id+"F5.wireOp",EDGE,"E55.MirrorCS");Q5=makeQuery(id+"F5.imprint","IMPRINT",FACE,{"disambiguationData":[TD([[makeQuery(id+"F5.imprint","IMPRINT",EDGE,{"derivedFrom":subQ0}),1.0]])]});}
            var Q6;
            {var subQ0=sQuery(id+"F5.wireOp",EDGE,"E102.MirrorCS");var subQ1=sQuery(id+"F5.wireOp",EDGE,"E57.MirrorCS");var subQ2=makeQuery(id+"F5.imprint","INTERSECT",VERTEX,{"derivedFrom":[subQ1,subQ0]});Q6=makeQuery(id+"F5.imprint","IMPRINT",FACE,{"disambiguationData":[TD([[makeQuery(id+"F5.imprint","IMPRINT",EDGE,{"disambiguationData":[TD([[subQ2,-1.0]])],"derivedFrom":subQ1}),1.0]])]});}
            var Q7;
            {var subQ0=sQuery(id+"F5.wireOp",EDGE,"E50.MirrorCS");Q7=makeQuery(id+"F5.imprint","IMPRINT",FACE,{"disambiguationData":[TD([[makeQuery(id+"F5.imprint","IMPRINT",EDGE,{"derivedFrom":subQ0}),1.0]])]});}
            var Q8;
            {var subQ0=sQuery(id+"F5.wireOp",EDGE,"E78.MirrorCS");var subQ1=sQuery(id+"F5.wireOp",EDGE,"E64.MirrorCS");var subQ2=makeQuery(id+"F5.imprint","INTERSECT",VERTEX,{"derivedFrom":[subQ1,subQ0]});Q8=makeQuery(id+"F5.imprint","IMPRINT",FACE,{"disambiguationData":[TD([[makeQuery(id+"F5.imprint","IMPRINT",EDGE,{"disambiguationData":[TD([[subQ2,-1.0]])],"derivedFrom":subQ1}),1.0]])]});}
            var Q9;
            {var subQ0=sQuery(id+"F5.wireOp",EDGE,"E52.MirrorCS");Q9=makeQuery(id+"F5.imprint","IMPRINT",FACE,{"disambiguationData":[TD([[makeQuery(id+"F5.imprint","IMPRINT",EDGE,{"derivedFrom":subQ0}),1.0]])]});}
            var Q10;
            {var subQ0=sQuery(id+"F5.wireOp",EDGE,"E98.MirrorCS");var subQ1=sQuery(id+"F5.wireOp",EDGE,"E89.MirrorCS");var subQ2=makeQuery(id+"F5.imprint","INTERSECT",VERTEX,{"derivedFrom":[subQ1,subQ0]});Q10=makeQuery(id+"F5.imprint","IMPRINT",FACE,{"disambiguationData":[TD([[makeQuery(id+"F5.imprint","IMPRINT",EDGE,{"disambiguationData":[TD([[subQ2,1.0]])],"derivedFrom":subQ1}),1.0]])]});}
            var Q11;
            {var subQ0=sQuery(id+"F5.wireOp",EDGE,"E51.MirrorCS");Q11=makeQuery(id+"F5.imprint","IMPRINT",FACE,{"disambiguationData":[TD([[makeQuery(id+"F5.imprint","IMPRINT",EDGE,{"derivedFrom":subQ0}),1.0]])]});}
            var Q12;
            {var subQ0=sQuery(id+"F5.wireOp",EDGE,"E107.MirrorCS");var subQ1=sQuery(id+"F5.wireOp",EDGE,"E59.MirrorCS");var subQ2=makeQuery(id+"F5.imprint","INTERSECT",VERTEX,{"derivedFrom":[subQ1,subQ0]});Q12=makeQuery(id+"F5.imprint","IMPRINT",FACE,{"disambiguationData":[TD([[makeQuery(id+"F5.imprint","IMPRINT",EDGE,{"disambiguationData":[TD([[subQ2,1.0]])],"derivedFrom":subQ1}),1.0]])]});}
            var Q13;
            {var subQ0=sQuery(id+"F5.wireOp",EDGE,"E56.MirrorCS");Q13=makeQuery(id+"F5.imprint","IMPRINT",FACE,{"disambiguationData":[TD([[makeQuery(id+"F5.imprint","IMPRINT",EDGE,{"derivedFrom":subQ0}),1.0]])]});}
            var Q14;
            {var subQ0=sQuery(id+"F5.wireOp",EDGE,"E104.MirrorCS");var subQ1=sQuery(id+"F5.wireOp",EDGE,"E103.MirrorCS");var subQ2=makeQuery(id+"F5.imprint","INTERSECT",VERTEX,{"derivedFrom":[subQ1,subQ0]});Q14=makeQuery(id+"F5.imprint","IMPRINT",FACE,{"disambiguationData":[TD([[makeQuery(id+"F5.imprint","IMPRINT",EDGE,{"disambiguationData":[TD([[subQ2,1.0]])],"derivedFrom":subQ1}),-1.0]])]});}
            var Q15;
            {var subQ0=sQuery(id+"F5.wireOp",EDGE,"E61.MirrorCS");Q15=makeQuery(id+"F5.imprint","IMPRINT",FACE,{"disambiguationData":[TD([[makeQuery(id+"F5.imprint","IMPRINT",EDGE,{"derivedFrom":subQ0}),-1.0]])]});}
            var Q16;
            {var subQ0=sQuery(id+"F5.wireOp",EDGE,"E54.MirrorCS");Q16=makeQuery(id+"F5.imprint","IMPRINT",FACE,{"disambiguationData":[TD([[makeQuery(id+"F5.imprint","IMPRINT",EDGE,{"derivedFrom":subQ0}),-1.0]])]});}
            var Q17;
            {var subQ0=sQuery(id+"F5.wireOp",EDGE,"E53.MirrorCS");Q17=makeQuery(id+"F5.imprint","IMPRINT",FACE,{"disambiguationData":[TD([[makeQuery(id+"F5.imprint","IMPRINT",EDGE,{"derivedFrom":subQ0}),-1.0]])]});}
            var Q18;
            {var subQ0=sQuery(id+"F5.wireOp",EDGE,"E93.MirrorCS");var subQ1=sQuery(id+"F5.wireOp",EDGE,"E85.MirrorCS");var subQ2=makeQuery(id+"F5.imprint","INTERSECT",VERTEX,{"derivedFrom":[subQ1,subQ0]});Q18=makeQuery(id+"F5.imprint","IMPRINT",FACE,{"disambiguationData":[TD([[makeQuery(id+"F5.imprint","IMPRINT",EDGE,{"disambiguationData":[TD([[subQ2,1.0]])],"derivedFrom":subQ1}),-1.0]])]});}
            var Q19;
            {var subQ0=sQuery(id+"F5.wireOp",EDGE,"E105.MirrorCS");var subQ1=sQuery(id+"F5.wireOp",EDGE,"E76.MirrorCS");var subQ2=makeQuery(id+"F5.imprint","INTERSECT",VERTEX,{"derivedFrom":[subQ1,subQ0]});Q19=makeQuery(id+"F5.imprint","IMPRINT",FACE,{"disambiguationData":[TD([[makeQuery(id+"F5.imprint","IMPRINT",EDGE,{"disambiguationData":[TD([[subQ2,-1.0]])],"derivedFrom":subQ1}),-1.0]])]});}
            var Q20;
            {var subQ0=sQuery(id+"F5.wireOp",EDGE,"E75.MirrorCS");var subQ1=sQuery(id+"F5.wireOp",EDGE,"E66.MirrorCS");var subQ2=makeQuery(id+"F5.imprint","INTERSECT",VERTEX,{"derivedFrom":[subQ1,subQ0]});Q20=makeQuery(id+"F5.imprint","IMPRINT",FACE,{"disambiguationData":[TD([[makeQuery(id+"F5.imprint","IMPRINT",EDGE,{"disambiguationData":[TD([[subQ2,1.0]])],"derivedFrom":subQ1}),-1.0]])]});}
            var Q21;
            {var subQ0=sQuery(id+"F5.wireOp",EDGE,"E80.MirrorCS");Q21=makeQuery(id+"F5.imprint","IMPRINT",FACE,{"disambiguationData":[TD([[makeQuery(id+"F5.imprint","IMPRINT",EDGE,{"derivedFrom":subQ0}),-1.0]])]});}
            var Q22;
            {var subQ0=sQuery(id+"F5.wireOp",EDGE,"E84.MirrorCS");var subQ1=sQuery(id+"F5.wireOp",EDGE,"E74.MirrorCS");var subQ2=makeQuery(id+"F5.imprint","INTERSECT",VERTEX,{"derivedFrom":[subQ1,subQ0]});Q22=makeQuery(id+"F5.imprint","IMPRINT",FACE,{"disambiguationData":[TD([[makeQuery(id+"F5.imprint","IMPRINT",EDGE,{"disambiguationData":[TD([[subQ2,-1.0]])],"derivedFrom":subQ1}),-1.0]])]});}
            var Q23;
            {var subQ0=sQuery(id+"F5.wireOp",EDGE,"E71.MirrorCS");Q23=makeQuery(id+"F5.imprint","IMPRINT",FACE,{"disambiguationData":[TD([[makeQuery(id+"F5.imprint","IMPRINT",EDGE,{"derivedFrom":subQ0}),-1.0]])]});}
            var Q24;
            {var subQ0=sQuery(id+"F5.wireOp",EDGE,"E94.MirrorCS");var subQ1=sQuery(id+"F5.wireOp",EDGE,"E70.MirrorCS");var subQ2=makeQuery(id+"F5.imprint","INTERSECT",VERTEX,{"derivedFrom":[subQ1,subQ0]});Q24=makeQuery(id+"F5.imprint","IMPRINT",FACE,{"disambiguationData":[TD([[makeQuery(id+"F5.imprint","IMPRINT",EDGE,{"disambiguationData":[TD([[subQ2,1.0]])],"derivedFrom":subQ1}),-1.0]])]});}
            var Q25;
            {var subQ0=sQuery(id+"F5.wireOp",EDGE,"E81.MirrorCS");Q25=makeQuery(id+"F5.imprint","IMPRINT",FACE,{"disambiguationData":[TD([[makeQuery(id+"F5.imprint","IMPRINT",EDGE,{"derivedFrom":subQ0}),-1.0]])]});}
            var Q26;
            {var subQ0=sQuery(id+"F5.wireOp",EDGE,"E18.9.0.6");var subQ1=sQuery(id+"F5.wireOp",EDGE,"E16.0");var subQ2=makeQuery(id+"F5.imprint","INTERSECT",VERTEX,{"derivedFrom":[subQ1,subQ0]});Q26=makeQuery(id+"F5.imprint","IMPRINT",FACE,{"disambiguationData":[TD([[makeQuery(id+"F5.imprint","IMPRINT",EDGE,{"disambiguationData":[TD([[subQ2,-1.0]])],"derivedFrom":subQ1}),1.0]])]});}
            var Q27;
            {var subQ5=sQuery(id+"F5.wireOp",EDGE,"E18.0.0.6");Q27=makeQuery(id+"F5.imprint","IMPRINT",FACE,{"disambiguationData":[TD([[makeQuery(id+"F5.imprint","IMPRINT",EDGE,{"derivedFrom":subQ5}),-1.0]])]});}
            var Q28;
            {var subQ5=sQuery(id+"F5.wireOp",EDGE,"E17.0.5.0");Q28=makeQuery(id+"F5.imprint","IMPRINT",FACE,{"disambiguationData":[TD([[makeQuery(id+"F5.imprint","IMPRINT",EDGE,{"derivedFrom":subQ5}),-1.0]])]});}
            var Q29;
            {var subQ0=sQuery(id+"F5.wireOp",EDGE,"E17.0.5.4");var subQ1=sQuery(id+"F5.wireOp",EDGE,"E16.0");var subQ2=makeQuery(id+"F5.imprint","INTERSECT",VERTEX,{"derivedFrom":[subQ1,subQ0]});Q29=makeQuery(id+"F5.imprint","IMPRINT",FACE,{"disambiguationData":[TD([[makeQuery(id+"F5.imprint","IMPRINT",EDGE,{"disambiguationData":[TD([[subQ2,-1.0]])],"derivedFrom":subQ1}),1.0]])]});}
            var Q30;
            {var subQ0=sQuery(id+"F5.wireOp",EDGE,"E17.0.4.4");var subQ1=sQuery(id+"F5.wireOp",EDGE,"E16.0");var subQ2=makeQuery(id+"F5.imprint","INTERSECT",VERTEX,{"derivedFrom":[subQ1,subQ0]});Q30=makeQuery(id+"F5.imprint","IMPRINT",FACE,{"disambiguationData":[TD([[makeQuery(id+"F5.imprint","IMPRINT",EDGE,{"disambiguationData":[TD([[subQ2,-1.0]])],"derivedFrom":subQ1}),1.0]])]});}
            var Q31;
            {var subQ5=sQuery(id+"F5.wireOp",EDGE,"E17.0.4.0");Q31=makeQuery(id+"F5.imprint","IMPRINT",FACE,{"disambiguationData":[TD([[makeQuery(id+"F5.imprint","IMPRINT",EDGE,{"derivedFrom":subQ5}),-1.0]])]});}
            var Q32;
            {var subQ5=sQuery(id+"F5.wireOp",EDGE,"E17.0.3.0");Q32=makeQuery(id+"F5.imprint","IMPRINT",FACE,{"disambiguationData":[TD([[makeQuery(id+"F5.imprint","IMPRINT",EDGE,{"derivedFrom":subQ5}),-1.0]])]});}
            var Q33;
            {var subQ0=sQuery(id+"F5.wireOp",EDGE,"E17.0.3.4");var subQ1=sQuery(id+"F5.wireOp",EDGE,"E16.0");var subQ2=makeQuery(id+"F5.imprint","INTERSECT",VERTEX,{"derivedFrom":[subQ1,subQ0]});Q33=makeQuery(id+"F5.imprint","IMPRINT",FACE,{"disambiguationData":[TD([[makeQuery(id+"F5.imprint","IMPRINT",EDGE,{"disambiguationData":[TD([[subQ2,-1.0]])],"derivedFrom":subQ1}),1.0]])]});}
            var Q34;
            {var subQ5=sQuery(id+"F5.wireOp",EDGE,"E17.0.2.0");Q34=makeQuery(id+"F5.imprint","IMPRINT",FACE,{"disambiguationData":[TD([[makeQuery(id+"F5.imprint","IMPRINT",EDGE,{"derivedFrom":subQ5}),-1.0]])]});}
            var Q35;
            {var subQ0=sQuery(id+"F5.wireOp",EDGE,"E17.0.2.4");var subQ1=sQuery(id+"F5.wireOp",EDGE,"E16.0");var subQ2=makeQuery(id+"F5.imprint","INTERSECT",VERTEX,{"derivedFrom":[subQ1,subQ0]});Q35=makeQuery(id+"F5.imprint","IMPRINT",FACE,{"disambiguationData":[TD([[makeQuery(id+"F5.imprint","IMPRINT",EDGE,{"disambiguationData":[TD([[subQ2,-1.0]])],"derivedFrom":subQ1}),1.0]])]});}
            var Q36;
            {var subQ5=sQuery(id+"F5.wireOp",EDGE,"E17.0.1.0");Q36=makeQuery(id+"F5.imprint","IMPRINT",FACE,{"disambiguationData":[TD([[makeQuery(id+"F5.imprint","IMPRINT",EDGE,{"derivedFrom":subQ5}),-1.0]])]});}
            var Q37;
            {var subQ0=sQuery(id+"F5.wireOp",EDGE,"E17.0.1.4");var subQ1=sQuery(id+"F5.wireOp",EDGE,"E16.0");var subQ2=makeQuery(id+"F5.imprint","INTERSECT",VERTEX,{"derivedFrom":[subQ1,subQ0]});Q37=makeQuery(id+"F5.imprint","IMPRINT",FACE,{"disambiguationData":[TD([[makeQuery(id+"F5.imprint","IMPRINT",EDGE,{"disambiguationData":[TD([[subQ2,-1.0]])],"derivedFrom":subQ1}),1.0]])]});}
            var Q38;
            {var subQ0=sQuery(id+"F5.wireOp",EDGE,"E15.0");Q38=makeQuery(id+"F5.imprint","IMPRINT",FACE,{"disambiguationData":[TD([[makeQuery(id+"F5.imprint","IMPRINT",EDGE,{"derivedFrom":subQ0}),-1.0]])]});}
            var Q39;
            {var subQ0=sQuery(id+"F5.wireOp",EDGE,"E15.2");var subQ1=sQuery(id+"F5.wireOp",EDGE,"E15.1");var subQ2=makeQuery(id+"F5.imprint","INTERSECT",VERTEX,{"derivedFrom":[subQ1,subQ0]});Q39=makeQuery(id+"F5.imprint","IMPRINT",FACE,{"disambiguationData":[TD([[makeQuery(id+"F5.imprint","IMPRINT",EDGE,{"disambiguationData":[TD([[subQ2,1.0]])],"derivedFrom":subQ1}),-1.0]])]});}
            var Q40;
            {var subQ0=sQuery(id+"F5.wireOp",EDGE,"E37.MirrorCS");var subQ1=sQuery(id+"F5.wireOp",EDGE,"E16.0");var subQ2=makeQuery(id+"F5.imprint","INTERSECT",VERTEX,{"derivedFrom":[subQ1,subQ0]});Q40=makeQuery(id+"F5.imprint","IMPRINT",FACE,{"disambiguationData":[TD([[makeQuery(id+"F5.imprint","IMPRINT",EDGE,{"disambiguationData":[TD([[subQ2,-1.0]])],"derivedFrom":subQ1}),1.0]])]});}
            var Q41;
            {var subQ5=sQuery(id+"F5.wireOp",EDGE,"E39.MirrorCS");Q41=makeQuery(id+"F5.imprint","IMPRINT",FACE,{"disambiguationData":[TD([[makeQuery(id+"F5.imprint","IMPRINT",EDGE,{"derivedFrom":subQ5}),1.0]])]});}
            var Q42;
            {var subQ5=sQuery(id+"F5.wireOp",EDGE,"E36.MirrorCS");Q42=makeQuery(id+"F5.imprint","IMPRINT",FACE,{"disambiguationData":[TD([[makeQuery(id+"F5.imprint","IMPRINT",EDGE,{"derivedFrom":subQ5}),1.0]])]});}
            var Q43;
            {var subQ0=sQuery(id+"F5.wireOp",EDGE,"E19.MirrorCS");var subQ1=sQuery(id+"F5.wireOp",EDGE,"E16.0");var subQ2=makeQuery(id+"F5.imprint","INTERSECT",VERTEX,{"derivedFrom":[subQ1,subQ0]});Q43=makeQuery(id+"F5.imprint","IMPRINT",FACE,{"disambiguationData":[TD([[makeQuery(id+"F5.imprint","IMPRINT",EDGE,{"disambiguationData":[TD([[subQ2,-1.0]])],"derivedFrom":subQ1}),1.0]])]});}
            var Q44;
            {var subQ0=sQuery(id+"F5.wireOp",EDGE,"E20.MirrorCS");var subQ1=sQuery(id+"F5.wireOp",EDGE,"E16.0");var subQ2=makeQuery(id+"F5.imprint","INTERSECT",VERTEX,{"derivedFrom":[subQ1,subQ0]});Q44=makeQuery(id+"F5.imprint","IMPRINT",FACE,{"disambiguationData":[TD([[makeQuery(id+"F5.imprint","IMPRINT",EDGE,{"disambiguationData":[TD([[subQ2,-1.0]])],"derivedFrom":subQ1}),1.0]])]});}
            var Q45;
            {var subQ5=sQuery(id+"F5.wireOp",EDGE,"E28.MirrorCS");Q45=makeQuery(id+"F5.imprint","IMPRINT",FACE,{"disambiguationData":[TD([[makeQuery(id+"F5.imprint","IMPRINT",EDGE,{"derivedFrom":subQ5}),1.0]])]});}
            var Q46;
            {var subQ5=sQuery(id+"F5.wireOp",EDGE,"E32.MirrorCS");Q46=makeQuery(id+"F5.imprint","IMPRINT",FACE,{"disambiguationData":[TD([[makeQuery(id+"F5.imprint","IMPRINT",EDGE,{"derivedFrom":subQ5}),1.0]])]});}
            var Q47;
            {var subQ0=sQuery(id+"F5.wireOp",EDGE,"E35.MirrorCS");var subQ1=sQuery(id+"F5.wireOp",EDGE,"E16.0");var subQ2=makeQuery(id+"F5.imprint","INTERSECT",VERTEX,{"derivedFrom":[subQ1,subQ0]});Q47=makeQuery(id+"F5.imprint","IMPRINT",FACE,{"disambiguationData":[TD([[makeQuery(id+"F5.imprint","IMPRINT",EDGE,{"disambiguationData":[TD([[subQ2,-1.0]])],"derivedFrom":subQ1}),1.0]])]});}
            var Q48;
            {var subQ0=sQuery(id+"F5.wireOp",EDGE,"E46.MirrorCS");var subQ1=sQuery(id+"F5.wireOp",EDGE,"E16.0");var subQ2=makeQuery(id+"F5.imprint","INTERSECT",VERTEX,{"derivedFrom":[subQ1,subQ0]});Q48=makeQuery(id+"F5.imprint","IMPRINT",FACE,{"disambiguationData":[TD([[makeQuery(id+"F5.imprint","IMPRINT",EDGE,{"disambiguationData":[TD([[subQ2,-1.0]])],"derivedFrom":subQ1}),1.0]])]});}
            var Q49;
            {var subQ5=sQuery(id+"F5.wireOp",EDGE,"E25.MirrorCS");Q49=makeQuery(id+"F5.imprint","IMPRINT",FACE,{"disambiguationData":[TD([[makeQuery(id+"F5.imprint","IMPRINT",EDGE,{"derivedFrom":subQ5}),1.0]])]});}
            var Q50;
            {var subQ1=sQuery(id+"F5.wireOp",EDGE,"E26.MirrorCS");Q50=makeQuery(id+"F5.imprint","IMPRINT",FACE,{"disambiguationData":[TD([[makeQuery(id+"F5.imprint","IMPRINT",EDGE,{"derivedFrom":subQ1}),1.0]])]});}
            var Q51;
            {var subQ3=sQuery(id+"F5.wireOp",EDGE,"E27.MirrorCS");var subQ5=sQuery(id+"F5.wireOp",EDGE,"E45.MirrorCS");var subQ6=makeQuery(id+"F5.imprint","INTERSECT",VERTEX,{"derivedFrom":[subQ3,subQ5]});Q51=makeQuery(id+"F5.imprint","IMPRINT",FACE,{"disambiguationData":[TD([[makeQuery(id+"F5.imprint","IMPRINT",EDGE,{"disambiguationData":[TD([[subQ6,-1.0]])],"derivedFrom":subQ3}),1.0]])]});}
            var Q52;
            Q52=makeQuery(id+"F1.opExtrude","SWEPT_FACE",FACE,{"disambiguationData":[OSD([sQuery(id+"F0.wireOp",EDGE,"E0.top")])]});
            extrude(context, id + "F8", {"entities" : qUnion([Q0, Q1, Q2, Q3, Q4, Q5, Q6, Q7, Q8, Q9, Q10, Q11, Q12, Q13, Q14, Q15, Q16, Q17, Q18, Q19, Q20, Q21, Q22, Q23, Q24, Q25, Q26, Q27, Q28, Q29, Q30, Q31, Q32, Q33, Q34, Q35, Q36, Q37, Q38, Q39, Q40, Q41, Q42, Q43, Q44, Q45, Q46, Q47, Q48, Q49, Q50, Q51]), "operationType" : NewBodyOperationType.REMOVE, "endBound" : BoundingType.UP_TO_SURFACE, "oppositeDirection" : true, "depth" : 25 * mm, "endBoundEntityFace" : qUnion([Q52]), "offsetDistance" : 25 * mm});
        }
        {
            var Q0;
            Q0=makeQuery(id+"F1.opExtrude","CAP_FACE",FACE,{"disambiguationData":[OSD([sQuery(id+"F0.wireOp",EDGE,"E0.bottom"),sQuery(id+"F0.wireOp",EDGE,"E0.top"),sQuery(id+"F0.wireOp",EDGE,"E0.left"),sQuery(id+"F0.wireOp",EDGE,"E0.right")])],"isStart":true});
            var sketch = newSketch(context, id + "F9", { "sketchPlane" : qUnion([Q0])});
            skLineSegment(sketch, "E116.0", {"start": v(22, 0) * mm, "end": v(22, -16) * mm});
            skLineSegment(sketch, "E117.0", {"start": v(0, 0) * mm, "end": v(22, 0) * mm});
            skLineSegment(sketch, "E118.0", {"start": v(0, 0) * mm, "end": v(0, -16) * mm});
            skLineSegment(sketch, "E119.0", {"start": v(0, -16) * mm, "end": v(22, -16) * mm});
            skSolve(sketch);
        }
        {
            var Q0;
            Q0=makeQuery(id+"F9.imprint","IMPRINT",FACE,{"disambiguationData":[TD([[makeQuery(id+"F9.imprint","IMPRINT",EDGE,{"derivedFrom":sQuery(id+"F9.wireOp",EDGE,"E116.0")}),-1.0]])]});
            extrude(context, id + "F10", {"entities" : qUnion([Q0]), "operationType" : NewBodyOperationType.REMOVE, "oppositeDirection" : true, "depth" : 25 * mm, "offsetDistance" : 25 * mm});
        }
    });
